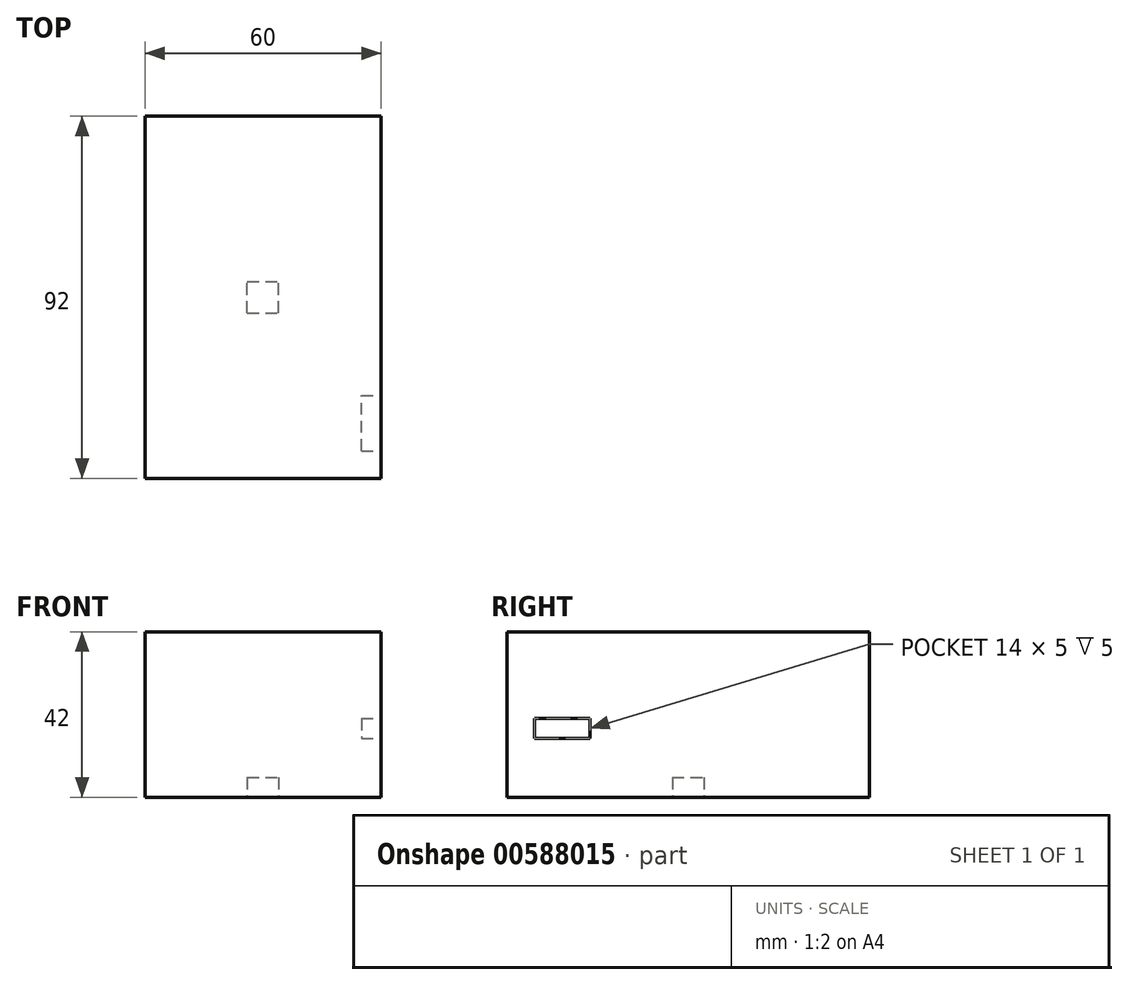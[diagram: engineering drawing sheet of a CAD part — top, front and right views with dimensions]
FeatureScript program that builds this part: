
annotation { "Feature Type Name" : "Feature", "Feature Type Description" : "" }
export const myFeature = defineFeature(function(context is Context, id is Id, definition is map)
    precondition{}
    {
        {
            var Q0;
            Q0=qCreatedBy(makeId("Top.planeOp"),FACE);
            var sketch = newSketch(context, id + "F0", { "sketchPlane" : qUnion([Q0])});
            skLineSegment(sketch, "E0.bottom", {"start": v(-29.39, 51.07) * mm, "end": v(30.61, 51.07) * mm});
            skLineSegment(sketch, "E0.top", {"start": v(-29.39, -40.93) * mm, "end": v(30.61, -40.93) * mm});
            skLineSegment(sketch, "E0.left", {"start": v(-29.39, 51.07) * mm, "end": v(-29.39, -40.93) * mm});
            skLineSegment(sketch, "E0.right", {"start": v(30.61, 51.07) * mm, "end": v(30.61, -40.93) * mm});
            skSolve(sketch);
        }
        {
            var Q0;
            Q0 = qSketchRegion(id + "F0", true);
            extrude(context, id + "F1", {"entities" : qUnion([Q0]), "depth" : 42 * mm, "offsetDistance" : 25 * mm});
        }
        {
            var Q0;
            Q0=makeQuery(id+"F1.opExtrude","CAP_FACE",FACE,{"disambiguationData":[OSD([sQuery(id+"F0.wireOp",EDGE,"E0.bottom"),sQuery(id+"F0.wireOp",EDGE,"E0.top"),sQuery(id+"F0.wireOp",EDGE,"E0.left"),sQuery(id+"F0.wireOp",EDGE,"E0.right")])],"isStart":true});
            var sketch = newSketch(context, id + "F2", { "sketchPlane" : qUnion([Q0])});
            skLineSegment(sketch, "E1.bottom", {"start": v(-3.39, -1.07) * mm, "end": v(4.61, -1.07) * mm});
            skLineSegment(sketch, "E1.top", {"start": v(-3.39, -9.07) * mm, "end": v(4.61, -9.07) * mm});
            skLineSegment(sketch, "E1.left", {"start": v(-3.39, -1.07) * mm, "end": v(-3.39, -9.07) * mm});
            skLineSegment(sketch, "E1.right", {"start": v(4.61, -1.07) * mm, "end": v(4.61, -9.07) * mm});
            skLineSegment(sketch, "E2", {"start": v(-3.39, -1.07) * mm, "end": v(-29.39, 40.93) * mm, "construction": true});
            skLineSegment(sketch, "E3", {"start": v(4.61, -1.07) * mm, "end": v(30.61, 40.93) * mm, "construction": true});
            skLineSegment(sketch, "E4", {"start": v(-29.39, -51.07) * mm, "end": v(-3.39, -9.07) * mm, "construction": true});
            skLineSegment(sketch, "E5", {"start": v(30.61, -51.07) * mm, "end": v(4.61, -9.07) * mm, "construction": true});
            skSolve(sketch);
        }
        {
            var Q0;
            Q0=makeQuery(id+"F2.imprint","IMPRINT",FACE,{"disambiguationData":[TD([[makeQuery(id+"F2.imprint","IMPRINT",EDGE,{"derivedFrom":sQuery(id+"F2.wireOp",EDGE,"E1.bottom")}),-1.0]])]});
            extrude(context, id + "F3", {"entities" : qUnion([Q0]), "operationType" : NewBodyOperationType.REMOVE, "oppositeDirection" : true, "depth" : 5 * mm, "offsetDistance" : 25 * mm});
        }
        {
            var Q0;
            Q0=makeQuery(id+"F1.opExtrude","SWEPT_FACE",FACE,{"disambiguationData":[OSD([sQuery(id+"F0.wireOp",EDGE,"E0.right")])]});
            var sketch = newSketch(context, id + "F4", { "sketchPlane" : qUnion([Q0])});
            skLineSegment(sketch, "E6.bottom", {"start": v(-33.93, 20) * mm, "end": v(-19.93, 20) * mm});
            skLineSegment(sketch, "E6.top", {"start": v(-33.93, 15) * mm, "end": v(-19.93, 15) * mm});
            skLineSegment(sketch, "E6.left", {"start": v(-33.93, 20) * mm, "end": v(-33.93, 15) * mm});
            skLineSegment(sketch, "E6.right", {"start": v(-19.93, 20) * mm, "end": v(-19.93, 15) * mm});
            skSolve(sketch);
        }
        {
            var Q0;
            Q0=makeQuery(id+"F4.imprint","IMPRINT",FACE,{"disambiguationData":[TD([[makeQuery(id+"F4.imprint","IMPRINT",EDGE,{"derivedFrom":sQuery(id+"F4.wireOp",EDGE,"E6.bottom")}),-1.0]])]});
            extrude(context, id + "F5", {"entities" : qUnion([Q0]), "operationType" : NewBodyOperationType.REMOVE, "oppositeDirection" : true, "depth" : 5 * mm, "offsetDistance" : 25 * mm});
        }
    });
